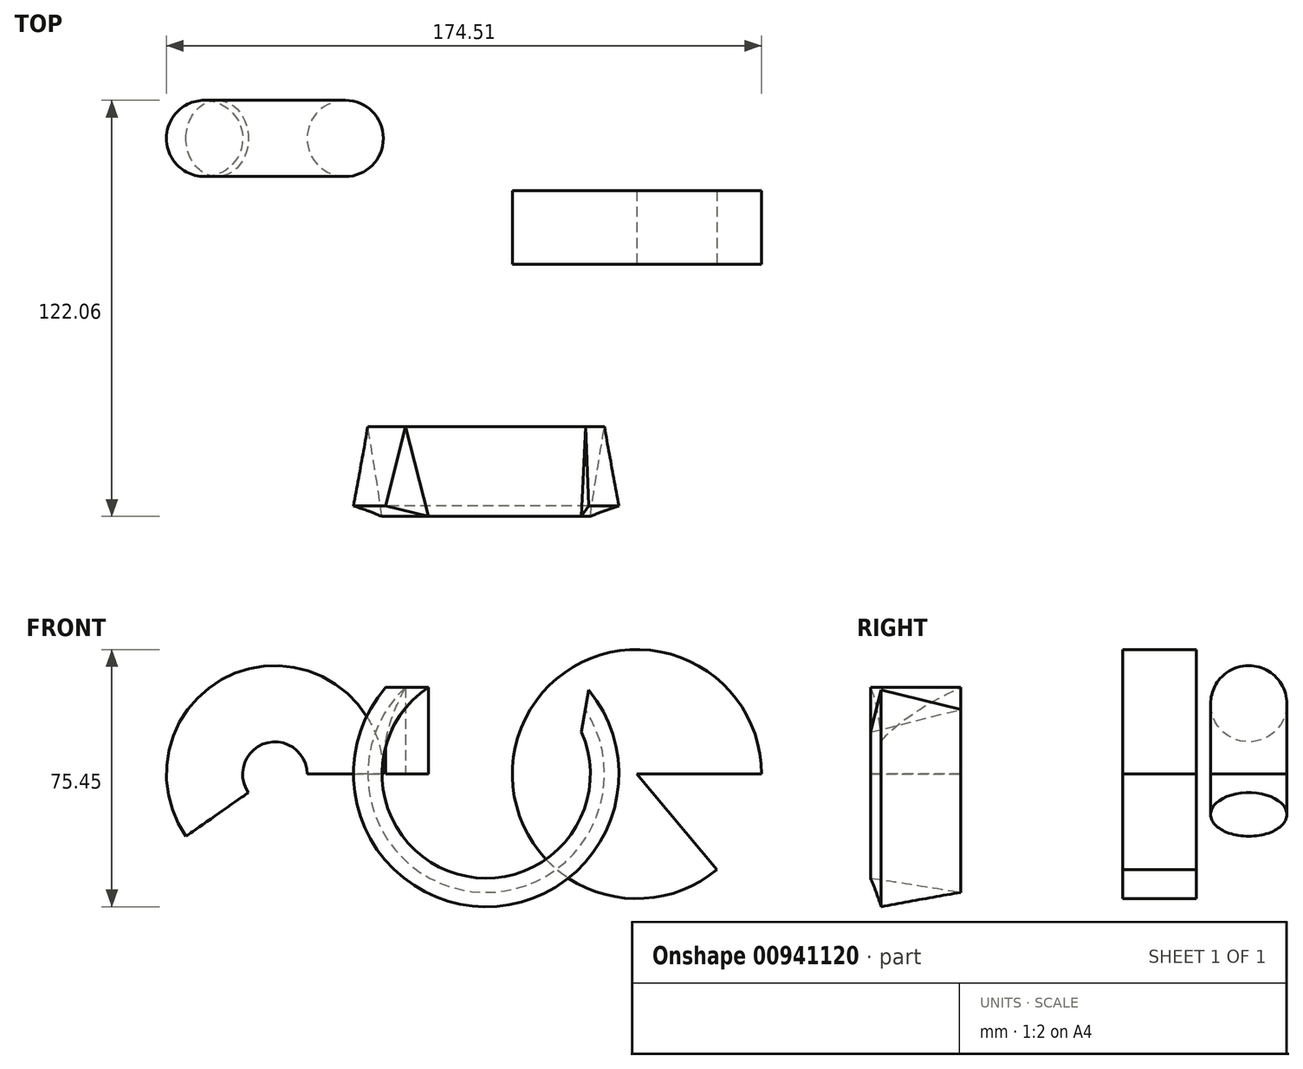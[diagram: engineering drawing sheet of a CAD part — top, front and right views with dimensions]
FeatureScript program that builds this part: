
annotation { "Feature Type Name" : "Feature", "Feature Type Description" : "" }
export const myFeature = defineFeature(function(context is Context, id is Id, definition is map)
    precondition{}
    {
        {
            var Q0;
            Q0=qCreatedBy(makeId("Top.planeOp"),FACE);
            var sketch = newSketch(context, id + "F0", { "sketchPlane" : qUnion([Q0])});
            skCircle(sketch, "E0", {"center": v(-62.28, 52.52) * mm, "radius": 11.18 * mm});
            skLineSegment(sketch, "E1.bottom", {"start": v(23.25, 37.16) * mm, "end": v(59.79, 37.16) * mm});
            skLineSegment(sketch, "E1.top", {"start": v(23.25, 15.57) * mm, "end": v(59.79, 15.57) * mm});
            skLineSegment(sketch, "E1.left", {"start": v(23.25, 37.16) * mm, "end": v(23.25, 15.57) * mm});
            skLineSegment(sketch, "E1.right", {"start": v(59.79, 37.16) * mm, "end": v(59.79, 15.57) * mm});
            skLineSegment(sketch, "E2", {"start": v(-55, -17.45) * mm, "end": v(-20.95, -29.08) * mm});
            skLineSegment(sketch, "E3", {"start": v(-20.95, -29.08) * mm, "end": v(-20.95, -63.13) * mm});
            skLineSegment(sketch, "E4", {"start": v(-20.95, -63.13) * mm, "end": v(-59.98, -69.35) * mm});
            skLineSegment(sketch, "E5", {"start": v(-59.98, -69.35) * mm, "end": v(-55, -17.45) * mm});
            skLineSegment(sketch, "E6", {"start": v(-44.62, -31.99) * mm, "end": v(-50.43, -55.24) * mm});
            skLineSegment(sketch, "E7", {"start": v(-50.43, -55.24) * mm, "end": v(-37.93, -58.36) * mm});
            skLineSegment(sketch, "E8", {"start": v(-37.93, -58.36) * mm, "end": v(-44.62, -31.99) * mm});
            skLineSegment(sketch, "E9", {"start": v(-82.91, 71.7) * mm, "end": v(-82.91, 30.26) * mm, "construction": true});
            skSolve(sketch);
        }
        {
            var Q0;
            Q0=makeQuery(id+"F0.imprint","IMPRINT",FACE,{"disambiguationData":[TD([[makeQuery(id+"F0.imprint","IMPRINT",EDGE,{"derivedFrom":sQuery(id+"F0.wireOp",EDGE,"E1.bottom")}),-1.0]])]});
            var Q1;
            Q1=sQuery(id+"F0.wireOp",EDGE,"E1.left");
            revolve(context, id + "F1", {"surfaceOperationType" : NewSurfaceOperationType.NEW, "entities" : qUnion([Q0]), "axis" : qUnion([Q1]), "revolveType" : RevolveType.ONE_DIRECTION, "angle" : 310 * degree});
        }
        {
            var Q0;
            Q0=makeQuery(id+"F0.imprint","IMPRINT",FACE,{"disambiguationData":[TD([[makeQuery(id+"F0.imprint","IMPRINT",EDGE,{"derivedFrom":sQuery(id+"F0.wireOp",EDGE,"E0")}),1.0]])]});
            var Q1;
            Q1=sQuery(id+"F0.wireOp",EDGE,"E9");
            revolve(context, id + "F2", {"surfaceOperationType" : NewSurfaceOperationType.NEW, "entities" : qUnion([Q0]), "axis" : qUnion([Q1]), "revolveType" : RevolveType.ONE_DIRECTION, "angle" : 215 * degree});
        }
        {
            var Q0;
            Q0=makeQuery(id+"F0.imprint","IMPRINT",FACE,{"disambiguationData":[TD([[makeQuery(id+"F0.imprint","IMPRINT",EDGE,{"derivedFrom":sQuery(id+"F0.wireOp",EDGE,"E6")}),1.0]])]});
            extrude(context, id + "F3", {"entities" : qUnion([Q0]), "depth" : 25.4 * mm, "offsetDistance" : 25.4 * mm});
        }
        {
            var Q0;
            Q0=makeQuery(id+"F3.opExtrude","CAP_FACE",FACE,{"disambiguationData":[OSD([sQuery(id+"F0.wireOp",EDGE,"E6"),sQuery(id+"F0.wireOp",EDGE,"E7"),sQuery(id+"F0.wireOp",EDGE,"E8")])],"isStart":false});
            var Q1;
            Q1=sQuery(id+"F0.wireOp",EDGE,"E3");
            revolve(context, id + "F4", {"operationType" : NewBodyOperationType.ADD, "surfaceOperationType" : NewSurfaceOperationType.NEW, "entities" : qUnion([Q0]), "axis" : qUnion([Q1]), "revolveType" : RevolveType.ONE_DIRECTION, "angle" : 260 * degree});
        }
    });
